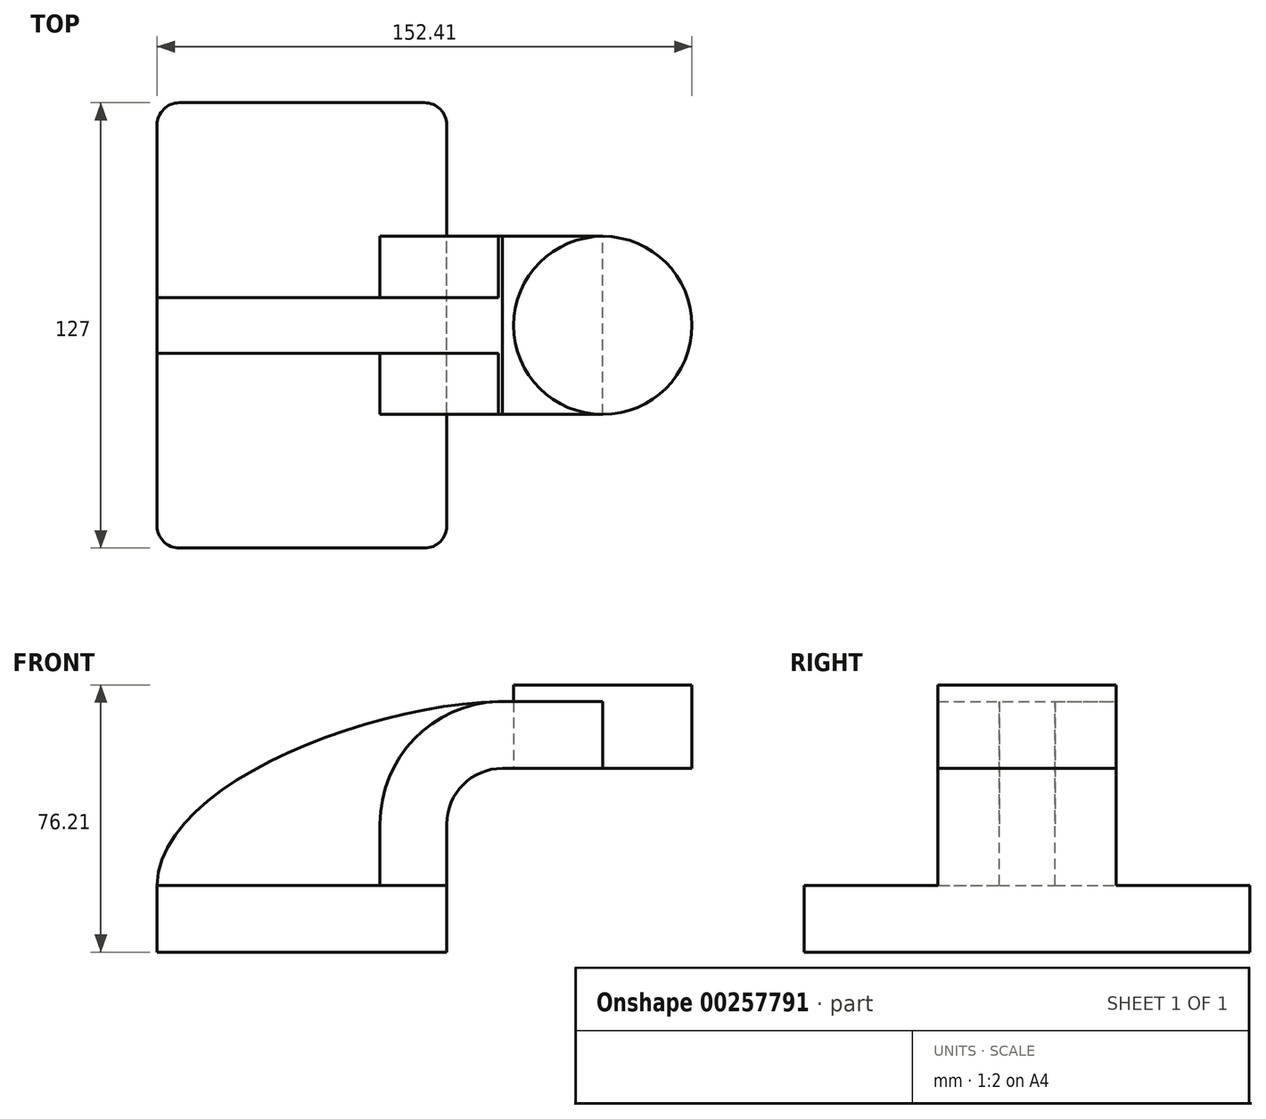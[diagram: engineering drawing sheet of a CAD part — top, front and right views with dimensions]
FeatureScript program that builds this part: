
annotation { "Feature Type Name" : "Feature", "Feature Type Description" : "" }
export const myFeature = defineFeature(function(context is Context, id is Id, definition is map)
    precondition{}
    {
        {
            var Q0;
            Q0=qCreatedBy(makeId("Front.planeOp"),FACE);
            var sketch = newSketch(context, id + "F0", { "sketchPlane" : qUnion([Q0])});
            skLineSegment(sketch, "E0.bottom", {"start": v(41.28, 9.53) * mm, "end": v(-41.28, 9.53) * mm});
            skLineSegment(sketch, "E0.top", {"start": v(41.28, -9.52) * mm, "end": v(-41.28, -9.53) * mm});
            skLineSegment(sketch, "E0.left", {"start": v(41.28, 9.53) * mm, "end": v(41.28, -9.52) * mm});
            skLineSegment(sketch, "E0.right", {"start": v(-41.28, 9.53) * mm, "end": v(-41.28, -9.53) * mm});
            skPoint(sketch, "E0.middle", {"position": v(0, 0) * mm});
            skLineSegment(sketch, "E1.bottom", {"start": v(111.12, 38.1) * mm, "end": v(60.33, 38.1) * mm});
            skLineSegment(sketch, "E1.top", {"start": v(111.12, 66.68) * mm, "end": v(60.33, 66.68) * mm});
            skLineSegment(sketch, "E1.left", {"start": v(111.12, 38.1) * mm, "end": v(111.12, 66.67) * mm});
            skLineSegment(sketch, "E1.right", {"start": v(60.33, 38.1) * mm, "end": v(60.33, 66.68) * mm});
            skPoint(sketch, "E1.middle", {"position": v(85.72, 52.39) * mm});
            skLineSegment(sketch, "E2", {"start": v(41.28, 9.53) * mm, "end": v(41.28, 27) * mm});
            skArc(sketch, "E3", {"start": v(41.27, 27) * mm, "mid": v(45.92, 38.23) * mm, "end": v(57.15, 42.88) * mm});
            skLineSegment(sketch, "E4", {"start": v(57.15, 42.88) * mm, "end": v(85.72, 42.88) * mm});
            skLineSegment(sketch, "E5.0", {"start": v(57.15, 61.93) * mm, "end": v(85.72, 61.93) * mm});
            skArc(sketch, "E5.1", {"start": v(22.22, 27) * mm, "mid": v(32.45, 51.7) * mm, "end": v(57.15, 61.93) * mm});
            skLineSegment(sketch, "E5.2", {"start": v(22.22, 9.53) * mm, "end": v(22.22, 27) * mm});
            skLineSegment(sketch, "E6", {"start": v(85.72, 42.88) * mm, "end": v(85.72, 66.68) * mm});
            skFitSpline(sketch, "E7", {"points": [v(-41.28, 9.53) * mm, v(57.15, 61.93) * mm], "startDerivative": vector(1.07, 86.9) * mm, "endDerivative": vector(111.7, 1.21) * mm});
            skLineSegment(sketch, "E8", {"start": v(85.72, 42.88) * mm, "end": v(111.12, 42.88) * mm});
            skSolve(sketch);
        }
        {
            var Q0;
            Q0=makeQuery(id+"F0.imprint","IMPRINT",FACE,{"disambiguationData":[TD([[makeQuery(id+"F0.imprint","IMPRINT",EDGE,{"derivedFrom":sQuery(id+"F0.wireOp",EDGE,"E0.top")}),-1.0]])]});
            extrude(context, id + "F1", {"entities" : qUnion([Q0]), "endBound" : BoundingType.SYMMETRIC, "depth" : 127 * mm});
        }
        {
            var Q0;
            {var subQ6=sQuery(id+"F0.wireOp",EDGE,"E2");Q0=makeQuery(id+"F0.imprint","IMPRINT",FACE,{"disambiguationData":[TD([[makeQuery(id+"F0.imprint","IMPRINT",EDGE,{"derivedFrom":subQ6}),1.0]])]});}
            var Q1;
            {var subQ0=sQuery(id+"F0.wireOp",EDGE,"E4");var subQ1=sQuery(id+"F0.wireOp",EDGE,"E1.right");var subQ2=makeQuery(id+"F0.imprint","INTERSECT",VERTEX,{"derivedFrom":[subQ1,subQ0]});Q1=makeQuery(id+"F0.imprint","IMPRINT",FACE,{"disambiguationData":[TD([[makeQuery(id+"F0.imprint","IMPRINT",EDGE,{"disambiguationData":[TD([[subQ2,-1.0]])],"derivedFrom":subQ1}),-1.0]])]});}
            extrude(context, id + "F2", {"entities" : qUnion([Q0, Q1]), "operationType" : NewBodyOperationType.ADD, "endBound" : BoundingType.SYMMETRIC, "depth" : 50.8 * mm});
        }
        {
            var Q0;
            {var subQ3=sQuery(id+"F0.wireOp",EDGE,"E5.2");Q0=makeQuery(id+"F0.imprint","IMPRINT",FACE,{"disambiguationData":[TD([[makeQuery(id+"F0.imprint","IMPRINT",EDGE,{"derivedFrom":subQ3}),1.0]])]});}
            extrude(context, id + "F3", {"entities" : qUnion([Q0]), "operationType" : NewBodyOperationType.ADD, "endBound" : BoundingType.SYMMETRIC, "depth" : 15.88 * mm});
        }
        {
            var Q0;
            {var subQ6=sQuery(id+"F0.wireOp",EDGE,"E8");Q0=makeQuery(id+"F0.imprint","IMPRINT",FACE,{"disambiguationData":[TD([[makeQuery(id+"F0.imprint","IMPRINT",EDGE,{"derivedFrom":subQ6}),1.0]])]});}
            var Q1;
            Q1=sQuery(id+"F0.wireOp",EDGE,"E6");
            revolve(context, id + "F4", {"entities" : qUnion([Q0]), "axis" : qUnion([Q1]), "revolveType" : RevolveType.FULL});
        }
        {
            var Q0;
            Q0=makeQuery(id+"F1.opExtrude","CAP_EDGE",EDGE,{"disambiguationData":[OSD([sQuery(id+"F0.wireOp",EDGE,"E0.right")])],"isStart":false});
            var Q1;
            Q1=makeQuery(id+"F1.opExtrude","CAP_EDGE",EDGE,{"disambiguationData":[OSD([sQuery(id+"F0.wireOp",EDGE,"E0.left")])],"isStart":false});
            var Q2;
            Q2=makeQuery(id+"F1.opExtrude","CAP_EDGE",EDGE,{"disambiguationData":[OSD([sQuery(id+"F0.wireOp",EDGE,"E0.right")])],"isStart":true});
            var Q3;
            Q3=makeQuery(id+"F1.opExtrude","CAP_EDGE",EDGE,{"disambiguationData":[OSD([sQuery(id+"F0.wireOp",EDGE,"E0.left")])],"isStart":true});
            fillet(context, id + "F5", {"entities" : qUnion([Q0, Q1, Q2, Q3]), "radius" : 6.35 * mm, "tangentPropagation" : true, "allowEdgeOverflow" : false});
        }
    });
